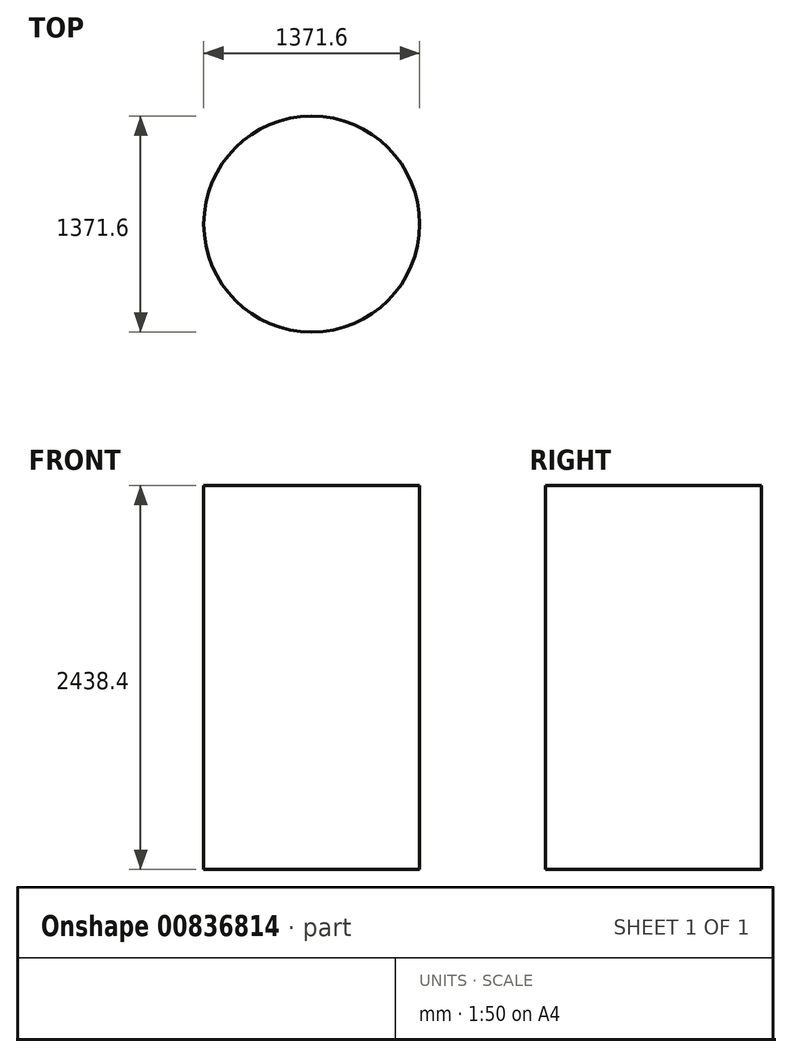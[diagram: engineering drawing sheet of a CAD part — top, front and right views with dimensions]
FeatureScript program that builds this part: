
annotation { "Feature Type Name" : "Feature", "Feature Type Description" : "" }
export const myFeature = defineFeature(function(context is Context, id is Id, definition is map)
    precondition{}
    {
        {
            var Q0;
            Q0=qCreatedBy(makeId("Top.planeOp"),FACE);
            var sketch = newSketch(context, id + "F0", { "sketchPlane" : qUnion([Q0])});
            skCircle(sketch, "E0", {"center": v(0, 0) * mm, "radius": 685.8 * mm});
            skSolve(sketch);
        }
        {
            var Q0;
            Q0 = qSketchRegion(id + "F0", true);
            extrude(context, id + "F1", {"entities" : qUnion([Q0]), "depth" : 2438.4 * mm, "offsetDistance" : 25.4 * mm});
        }
    });
